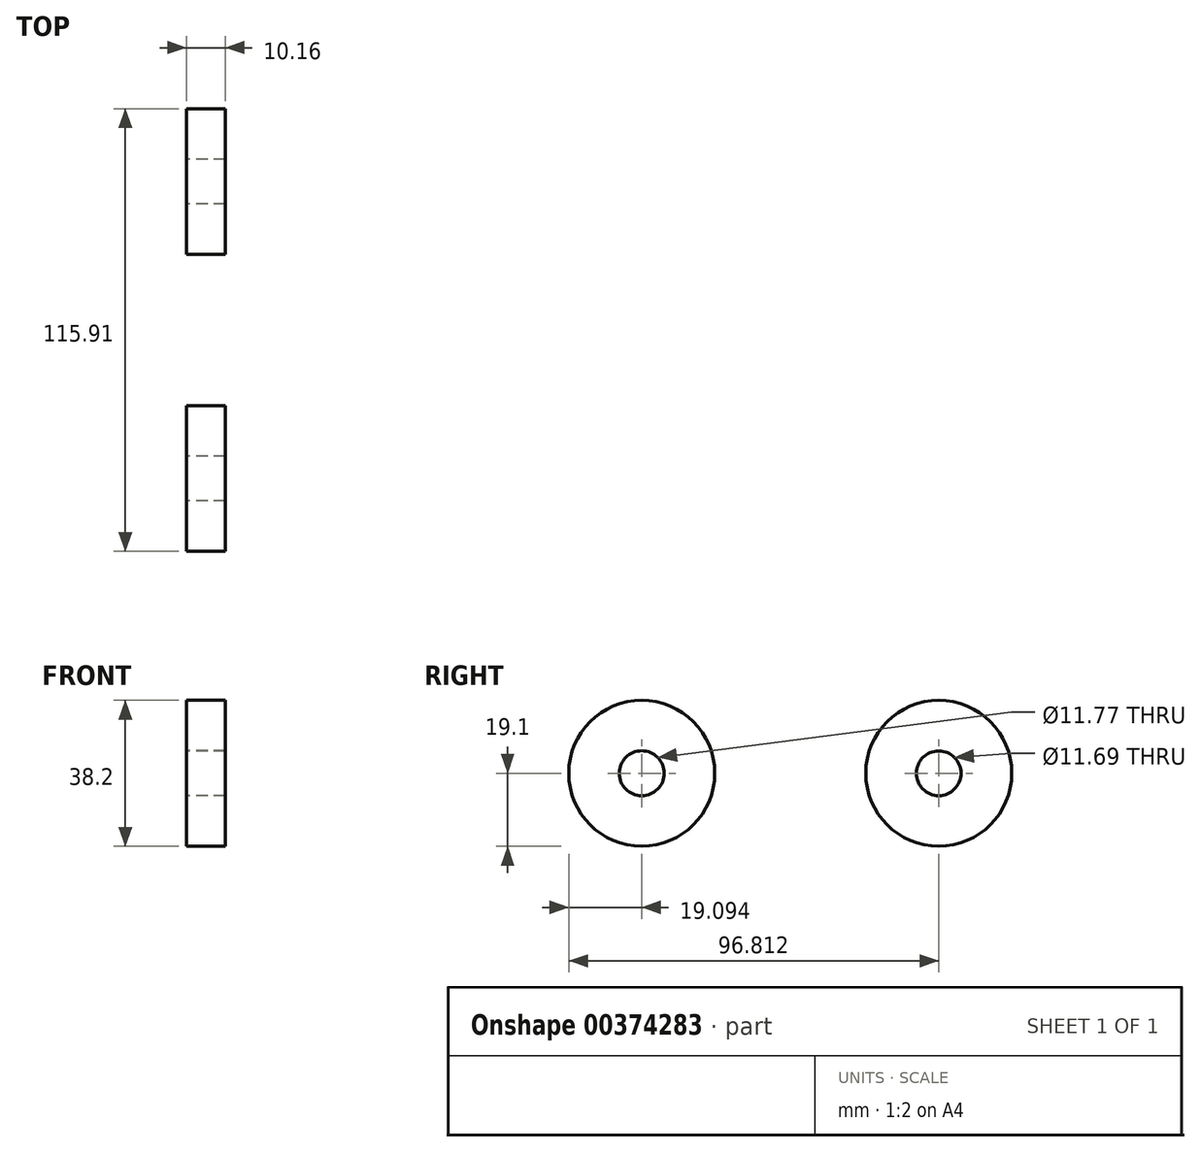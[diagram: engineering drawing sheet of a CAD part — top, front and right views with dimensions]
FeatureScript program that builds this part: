
annotation { "Feature Type Name" : "Feature", "Feature Type Description" : "" }
export const myFeature = defineFeature(function(context is Context, id is Id, definition is map)
    precondition{}
    {
        {
            var Q0;
            Q0=qCreatedBy(makeId("Right.planeOp"),FACE);
            var sketch = newSketch(context, id + "F0", { "sketchPlane" : qUnion([Q0])});
            skCircle(sketch, "E0", {"center": v(-37.24, 0) * mm, "radius": 19.1 * mm});
            skCircle(sketch, "E1", {"center": v(40.48, 0) * mm, "radius": 19.1 * mm});
            skCircle(sketch, "E2", {"center": v(-37.24, 0) * mm, "radius": 5.88 * mm});
            skCircle(sketch, "E3", {"center": v(40.48, 0) * mm, "radius": 5.85 * mm});
            skSolve(sketch);
        }
        {
            var Q0;
            Q0=makeQuery(id+"F0.imprint","IMPRINT",FACE,{"disambiguationData":[TD([[makeQuery(id+"F0.imprint","IMPRINT",EDGE,{"derivedFrom":sQuery(id+"F0.wireOp",EDGE,"E0")}),1.0]])]});
            var Q1;
            Q1=makeQuery(id+"F0.imprint","IMPRINT",FACE,{"disambiguationData":[TD([[makeQuery(id+"F0.imprint","IMPRINT",EDGE,{"derivedFrom":sQuery(id+"F0.wireOp",EDGE,"E1")}),1.0]])]});
            extrude(context, id + "F1", {"entities" : qUnion([Q0, Q1]), "depth" : 10.16 * mm});
        }
    });
